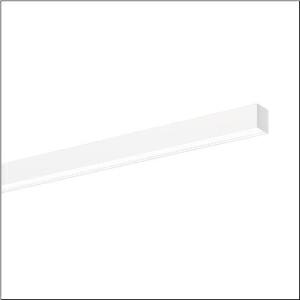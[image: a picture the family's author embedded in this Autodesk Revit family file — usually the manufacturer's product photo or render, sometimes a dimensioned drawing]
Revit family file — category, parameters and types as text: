
# Revit family: silica_r__21_51mx23dc3awb_8ef9
name_source: partatom
category: Lighting Fixtures
units: mm (PartAtom-declared; Revit-internal decimal feet)

## family parameters
Cut with Voids When Loaded = No
Host = Face
Light Source = No
Part Type = Normal
Room Calculation Point = No
Round Connector Dimension = Use Diameter
Shared = No

## types (1)
- --- (1 x LED, 8200 lm, 62.2 W, 3000K)
    Apparent Load = 62 VA
    CIE Flux Codes = 78 96 99 100 100
    Color Rendering = 80
    Color Temperature = 3000K
    Default Elevation = 1800 mm
    Description = Silica® 21, office luminaire, primary optical cover: prismatic diffuser, of PMMA, CAT 2 (L<= 3000cd/m²), light emission: direct distribution, primary light characteristic: symmetric, installation type: surface-mounted, LED, rated luminous flux: 8.200lm, luminous efficacy: 132lm/W, light colour: 830, colour temperature: 3000K, with terminal, 3+2-pole, max. 2.5mm², mains connection: 220..240V, AC, 50/60Hz, rated input power: 62.2W, luminaire housing, of aluminium, traffic white (RAL 9016), length: 3.004mm, width: 53mm, height: 53mm, protection rating (complete): IP20, insulation class (complete): insulation class I (protective earthing), certification: CE, permissible operating ambient temperature: 0..+35°C, standard: EN 50419, packaging unit: 1 piece
    Height = 0 mm  [stored 0 ft]
    Lamp = 1 x LED
    Lamp Light Flux = 8200 lm
    Lamp Power = 62.2 W
    Lamp count = 1
    Length = 3004 mm
    Luminous efficacy = 132 lm/W
    Manufacturer = Siteco
    ModVariant = No
    Model = 51MX23DC3AWB
    Mounting Place = Ceiling
    Mounting Type = Recessed
    Number of Poles = 1
    OnlyDefault = Yes
    Power Factor = 1
    Product Name = Silica® 21
    Product group = office luminaire | ceiling recessed
    ProductGroupID = 401
    Protection Class = Protection class I
    Protection Degree = IP 20
    RLX_Detail_Level = 1
    RLX_Emergency_Light_Flux = 0 lm
    RLX_Emergency_Type = 0
    RLX_Emergency_Type_DB = No
    RlxData = <blob elided: 18705 chars, md5=916bcaab>
    Socket = socket
    Standby Power = 0 W
    System Light Flux = 8200 lm
    System Power = 62 W
    Type Comments = factory setting: luminous flux: 100 % | dim-lin: 254 | 345 mA
    Type Image = l_1313601.jpg
    URL = http://relux.com
    VarID = @adj_068233
    Voltage = 0 V
    Weight = 0.00 kg
    Width = 53 mm

note: [stored X ft] marks values corroborated as IEEE doubles in the binary element streams (Revit-internal decimal feet)

## geometry (parser evidence)
native form markers: Blend x4, Sweep x13
no freeform markers — native parametric forms only
